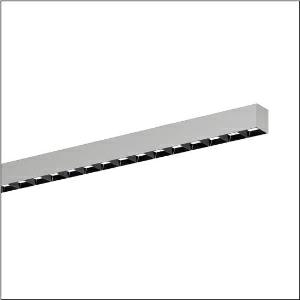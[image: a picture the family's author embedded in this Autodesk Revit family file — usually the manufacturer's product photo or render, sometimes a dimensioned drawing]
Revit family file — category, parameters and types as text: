
# Revit family: silica_r__21_51mx21tat4s_03ed
name_source: partatom
category: Lighting Fixtures
units: mm (PartAtom-declared; Revit-internal decimal feet)

## family parameters
Cut with Voids When Loaded = No
Host = Face
Light Source = No
Part Type = Normal
Room Calculation Point = No
Round Connector Dimension = Use Diameter
Shared = No

## types (1)
- --- (1 x LED, 3720 lm, 32.2 W, 6500K)
    Apparent Load = 32 VA
    CIE Flux Codes = 85 99 100 100 100
    Color Rendering = 80
    Color Temperature = 6500K
    Default Elevation = 1800 mm
    Description = Silica® 21, office luminaire, primary light control with darklight reflector, of PMMA, black, CAT 2 (L<= 3000cd/m²), light emission: direct distribution, primary light characteristic: symmetric, installation type: surface-mounted, LED, rated luminous flux: 3.720lm, luminous efficacy: 110lm/W, light colour: 8tw, colour temperature: 2700..6500K, control gear: ECG DALI, with terminal, 3+2-pole, max. 2.5mm², mains connection: 220..240V, AC, 50/60Hz, rated input power: 33.8W, luminaire housing, of aluminium, metallic grey (RAL 9006), length: 1.204mm, width: 53mm, height: 53mm, protection rating (complete): IP20, insulation class (complete): insulation class I (protective earthing), certification: CE, permissible operating ambient temperature: 0..+35°C, standard: EN 50419, packaging unit: 1 piece
    Height = 0 mm  [stored 0 ft]
    Lamp = 1 x LED
    Lamp Light Flux = 3720 lm
    Lamp Power = 32.2 W
    Lamp count = 1
    Length = 1204 mm
    Luminous efficacy = 116 lm/W
    Manufacturer = Siteco
    ModVariant = No
    Model = 51MX21TAT4S
    Mounting Place = Ceiling
    Mounting Type = Recessed
    Number of Poles = 1
    OnlyDefault = Yes
    Power Factor = 1
    Product Name = Silica® 21
    Product group = office luminaire | ceiling recessed
    ProductGroupID = 401
    Protection Class = Protection class I
    Protection Degree = IP 20
    RLX_Detail_Level = 1
    RLX_Emergency_Light_Flux = 0 lm
    RLX_Emergency_Type = 0
    RLX_Emergency_Type_DB = No
    RlxData = <blob elided: 39333 chars, md5=b81c1b9b>
    Socket = socket
    Standby Power = 0 W
    System Light Flux = 3720 lm
    System Power = 32 W
    Type Comments = individual setting
    Type Image = l_1297764.jpg
    URL = http://relux.com
    VarID = @adj_071377
    Voltage = 0 V
    Weight = 0.00 kg
    Width = 53 mm

note: [stored X ft] marks values corroborated as IEEE doubles in the binary element streams (Revit-internal decimal feet)

## geometry (parser evidence)
native form markers: Blend x4, Sweep x9
no freeform markers — native parametric forms only
